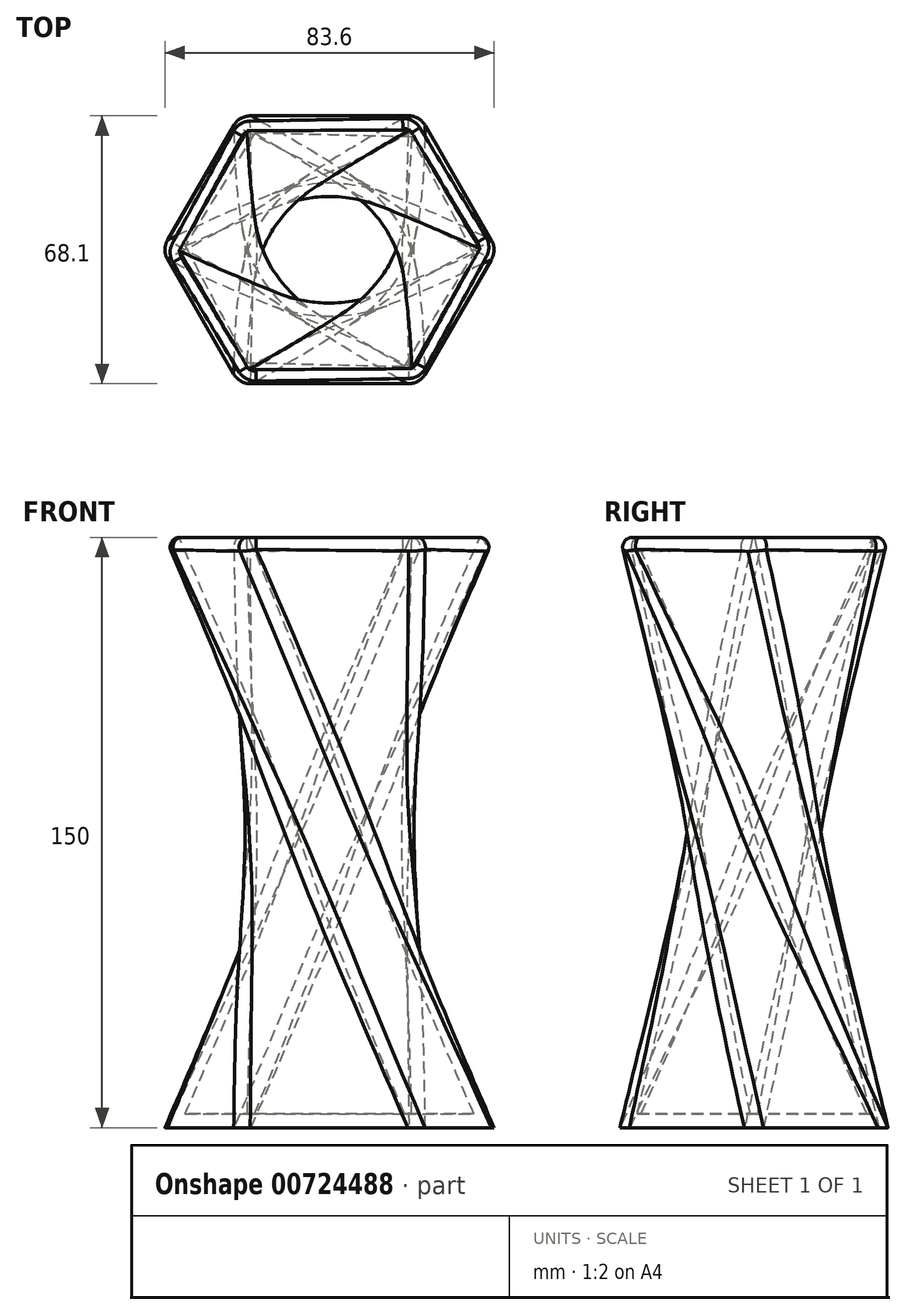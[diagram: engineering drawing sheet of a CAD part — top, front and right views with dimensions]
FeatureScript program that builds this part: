
annotation { "Feature Type Name" : "Feature", "Feature Type Description" : "" }
export const myFeature = defineFeature(function(context is Context, id is Id, definition is map)
    precondition{}
    {
        {
            var Q0;
            Q0=qCreatedBy(makeId("Top.planeOp"),FACE);
            var sketch = newSketch(context, id + "F0", { "sketchPlane" : qUnion([Q0])});
            skLineSegment(sketch, "E0", {"start": v(-40.34, 0) * mm, "end": v(44.74, 0) * mm, "construction": true});
            skLineSegment(sketch, "E1", {"start": v(0, 34.04) * mm, "end": v(0, -39.6) * mm, "construction": true});
            skLineSegment(sketch, "E2", {"start": v(-40.34, 0) * mm, "end": v(-20.68, 34.04) * mm});
            skLineSegment(sketch, "E3", {"start": v(-20.68, 34.04) * mm, "end": v(25.08, 34.04) * mm});
            skLineSegment(sketch, "E4", {"start": v(25.08, 34.04) * mm, "end": v(44.74, 0) * mm});
            skLineSegment(sketch, "E5.MirrorCS", {"start": v(-40.34, 0) * mm, "end": v(-20.68, -34.04) * mm});
            skLineSegment(sketch, "E6.MirrorCS", {"start": v(-20.68, -34.04) * mm, "end": v(25.08, -34.04) * mm});
            skLineSegment(sketch, "E7.MirrorCS", {"start": v(25.08, -34.04) * mm, "end": v(44.74, 0) * mm});
            skSolve(sketch);
        }
        {
            var Q0;
            Q0=qCreatedBy(makeId("Top.planeOp"),FACE);
            cPlane(context, id + "F1", {"entities" : qUnion([Q0]), "cplaneType" : CPlaneType.OFFSET, "offset" : 150 * mm, "width" : 150 * mm, "height" : 150 * mm});
        }
        {
            var Q0;
            Q0=qCreatedBy(id+"F1.planeOp",FACE);
            var sketch = newSketch(context, id + "F2", { "sketchPlane" : qUnion([Q0])});
            skLineSegment(sketch, "E8.0.0", {"start": v(-20.68, -34.04) * mm, "end": v(25.08, -34.04) * mm});
            skLineSegment(sketch, "E8.0.1", {"start": v(25.08, -34.04) * mm, "end": v(44.74, 0) * mm});
            skLineSegment(sketch, "E8.0.2", {"start": v(44.74, 0) * mm, "end": v(25.08, 34.04) * mm});
            skLineSegment(sketch, "E8.0.3", {"start": v(25.08, 34.04) * mm, "end": v(-20.68, 34.04) * mm});
            skLineSegment(sketch, "E8.0.4", {"start": v(-20.68, 34.04) * mm, "end": v(-40.34, 0) * mm});
            skLineSegment(sketch, "E8.0.5", {"start": v(-40.34, 0) * mm, "end": v(-20.68, -34.04) * mm});
            skSolve(sketch);
        }
        {
            var Q0;
            Q0=makeQuery(id+"F0.imprint","IMPRINT",FACE,{"disambiguationData":[TD([[makeQuery(id+"F0.imprint","IMPRINT",EDGE,{"derivedFrom":sQuery(id+"F0.wireOp",EDGE,"E2")}),-1.0]])]});
            var Q1;
            Q1=makeQuery(id+"F2.imprint","IMPRINT",FACE,{"disambiguationData":[TD([[makeQuery(id+"F2.imprint","IMPRINT",EDGE,{"derivedFrom":sQuery(id+"F2.wireOp",EDGE,"E8.0.0")}),1.0]])]});
            var Q2;
            Q2=sQuery(id+"F2.wireOp",VERTEX,"E8.0.0.end");
            var Q3;
            Q3=sQuery(id+"F0.wireOp",VERTEX,"E4.start");
            loft(context, id + "F3", {"sheetProfilesArray" : [{ "sheetProfileEntities" : qUnion([Q0]) }, { "sheetProfileEntities" : qUnion([Q1]) }], "matchConnections" : true, "connections" : [{ "connectionEntities" : qUnion([Q2, Q3]), "connectionEdgeQueries" : qUnion([]), "connectionEdgeParameters" : [] }]});
        }
        {
            var Q0;
            Q0=makeQuery(id+"F3.opLoft","CAP_FACE",FACE,{"disambiguationData":[OSD([makeQuery(id+"F2.imprint","IMPRINT",FACE,{"disambiguationData":[TD([[makeQuery(id+"F2.imprint","IMPRINT",EDGE,{"derivedFrom":sQuery(id+"F2.wireOp",EDGE,"E8.0.0")}),1.0]])]})])],"isStart":true});
            shell(context, id + "F4", {"entities" : qUnion([Q0]), "thickness" : 3.5 * mm});
        }
        {
            var Q0;
            Q0=makeQuery(id+"F3.opLoft","SWEPT_EDGE",EDGE,{"disambiguationData":[OSD([sQuery(id+"F0.wireOp",EDGE,"E4"),sQuery(id+"F0.wireOp",EDGE,"E7.MirrorCS"),sQuery(id+"F2.wireOp",EDGE,"E8.0.0"),sQuery(id+"F2.wireOp",EDGE,"E8.0.5")])]});
            var Q1;
            Q1=makeQuery(id+"F3.opLoft","SWEPT_EDGE",EDGE,{"disambiguationData":[OSD([sQuery(id+"F0.wireOp",EDGE,"E3"),sQuery(id+"F0.wireOp",EDGE,"E4"),sQuery(id+"F2.wireOp",EDGE,"E8.0.0"),sQuery(id+"F2.wireOp",EDGE,"E8.0.1")])]});
            var Q2;
            Q2=makeQuery(id+"F3.opLoft","SWEPT_EDGE",EDGE,{"disambiguationData":[OSD([sQuery(id+"F0.wireOp",EDGE,"E2"),sQuery(id+"F0.wireOp",EDGE,"E3"),sQuery(id+"F2.wireOp",EDGE,"E8.0.1"),sQuery(id+"F2.wireOp",EDGE,"E8.0.2")])]});
            var Q3;
            Q3=makeQuery(id+"F3.opLoft","SWEPT_EDGE",EDGE,{"disambiguationData":[OSD([sQuery(id+"F0.wireOp",EDGE,"E2"),sQuery(id+"F0.wireOp",EDGE,"E5.MirrorCS"),sQuery(id+"F2.wireOp",EDGE,"E8.0.2"),sQuery(id+"F2.wireOp",EDGE,"E8.0.3")])]});
            var Q4;
            Q4=makeQuery(id+"F3.opLoft","SWEPT_EDGE",EDGE,{"disambiguationData":[OSD([sQuery(id+"F0.wireOp",EDGE,"E5.MirrorCS"),sQuery(id+"F0.wireOp",EDGE,"E6.MirrorCS"),sQuery(id+"F2.wireOp",EDGE,"E8.0.3"),sQuery(id+"F2.wireOp",EDGE,"E8.0.4")])]});
            var Q5;
            Q5=makeQuery(id+"F3.opLoft","SWEPT_EDGE",EDGE,{"disambiguationData":[OSD([sQuery(id+"F0.wireOp",EDGE,"E6.MirrorCS"),sQuery(id+"F0.wireOp",EDGE,"E7.MirrorCS"),sQuery(id+"F2.wireOp",EDGE,"E8.0.4"),sQuery(id+"F2.wireOp",EDGE,"E8.0.5")])]});
            fillet(context, id + "F5", {"entities" : qUnion([Q0, Q1, Q2, Q3, Q4, Q5]), "radius" : 5 * mm, "tangentPropagation" : true, "allowEdgeOverflow" : false});
        }
        {
            var Q0;
            Q0=makeQuery(id+"F3.opLoft","MID_CAP_EDGE",EDGE,{"disambiguationData":[OSD([sQuery(id+"F2.wireOp",EDGE,"E8.0.0"),sQuery(id+"F2.wireOp",EDGE,"E8.0.4"),sQuery(id+"F2.wireOp",EDGE,"E8.0.5")])],"capPos":1.0});
            fillet(context, id + "F6", {"entities" : qUnion([Q0]), "radius" : 2.5 * mm, "tangentPropagation" : true, "allowEdgeOverflow" : false});
        }
    });
